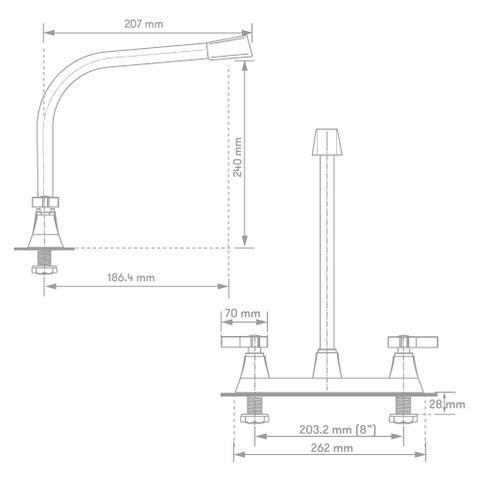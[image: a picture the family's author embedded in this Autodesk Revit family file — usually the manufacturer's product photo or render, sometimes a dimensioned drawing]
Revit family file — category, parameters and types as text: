
# Revit family: 01-1466-11 MEZCLADOR LAVAPLATOS 8” COBRA - TOSCANA
name_source: partatom
category: Plumbing Fixtures
revit_build: Autodesk Revit 2018 (Build: 20170223_1515(x64)
units: mm (PartAtom-declared; Revit-internal decimal feet)

## family parameters
Cut with Voids When Loaded = No
Host = Face
OmniClass Number = 23.31.11.00
Part Type = Normal
Room Calculation Point = No
Round Connector Dimension = Use Diameter
Shared = No

## types (1)
- 01-1466-11
    Alto = 273 mm
    Alto Aireador = 247 mm
    Ancho brazo = 182 mm
    Ancho entre manijas = 203.2 mm  [stored 0.666667 ft]
    Ancho manija = 70 mm
    CW Connection = Yes
    Default Elevation = 0 mm  [stored 0 ft]
    Description = Bimando
    HW Connection = Yes
    Link Ficha Tecnica = http://infotecnica.gricol.com
    Manufacturer = Gricol
    Model = 01-1466-11
    Plástico - ABS Cromado = Plastico - ABS Cromado
    Product Name = MEZCLADOR LAVAPLATOS 8” COBRA - TOSCANA
    Type Image = MEZCLADOR LAVAPLATOS 8” COBRA - TOSCANA.jpg
    URL = https://www.gricol.com
    Vent Connection = No
    Waste Connection = No

note: [stored X ft] marks values corroborated as IEEE doubles in the binary element streams (Revit-internal decimal feet)

## geometry (parser evidence)
native form markers: Blend x2, Sweep x4
no freeform markers — native parametric forms only
